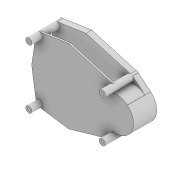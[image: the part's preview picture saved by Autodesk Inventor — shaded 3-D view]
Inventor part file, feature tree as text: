
AUTODESK INVENTOR PART (.ipt)
format: ipt  version: 2020 (Build 240168000, 168)  size: 253,440 bytes
history: native  units: mm
features: extrude x5, sketch x5, other x1, projected_geometry x1
ambient origin geometry x8: Origin, YZ Plane, XZ Plane, XY Plane, X Axis, Y Axis, Z Axis, Center Point
bodies: Body1 (feature_tree)
feature tree (12):
  other  "솔리드1"
  extrude  "돌출1"  Depth=35.14mm
  extrude  "돌출2"  Depth=96.74mm
  extrude  "돌출3"  Depth=70.28mm
  extrude  "돌출4"  Depth=27.87mm
  extrude  "돌출5"  Depth=42.0mm
  sketch  "스케치1"
  sketch  "스케치2"
  sketch  "스케치3"
  sketch  "스케치4"
  sketch  "스케치5"
  projected_geometry  "투영된 루프1"
